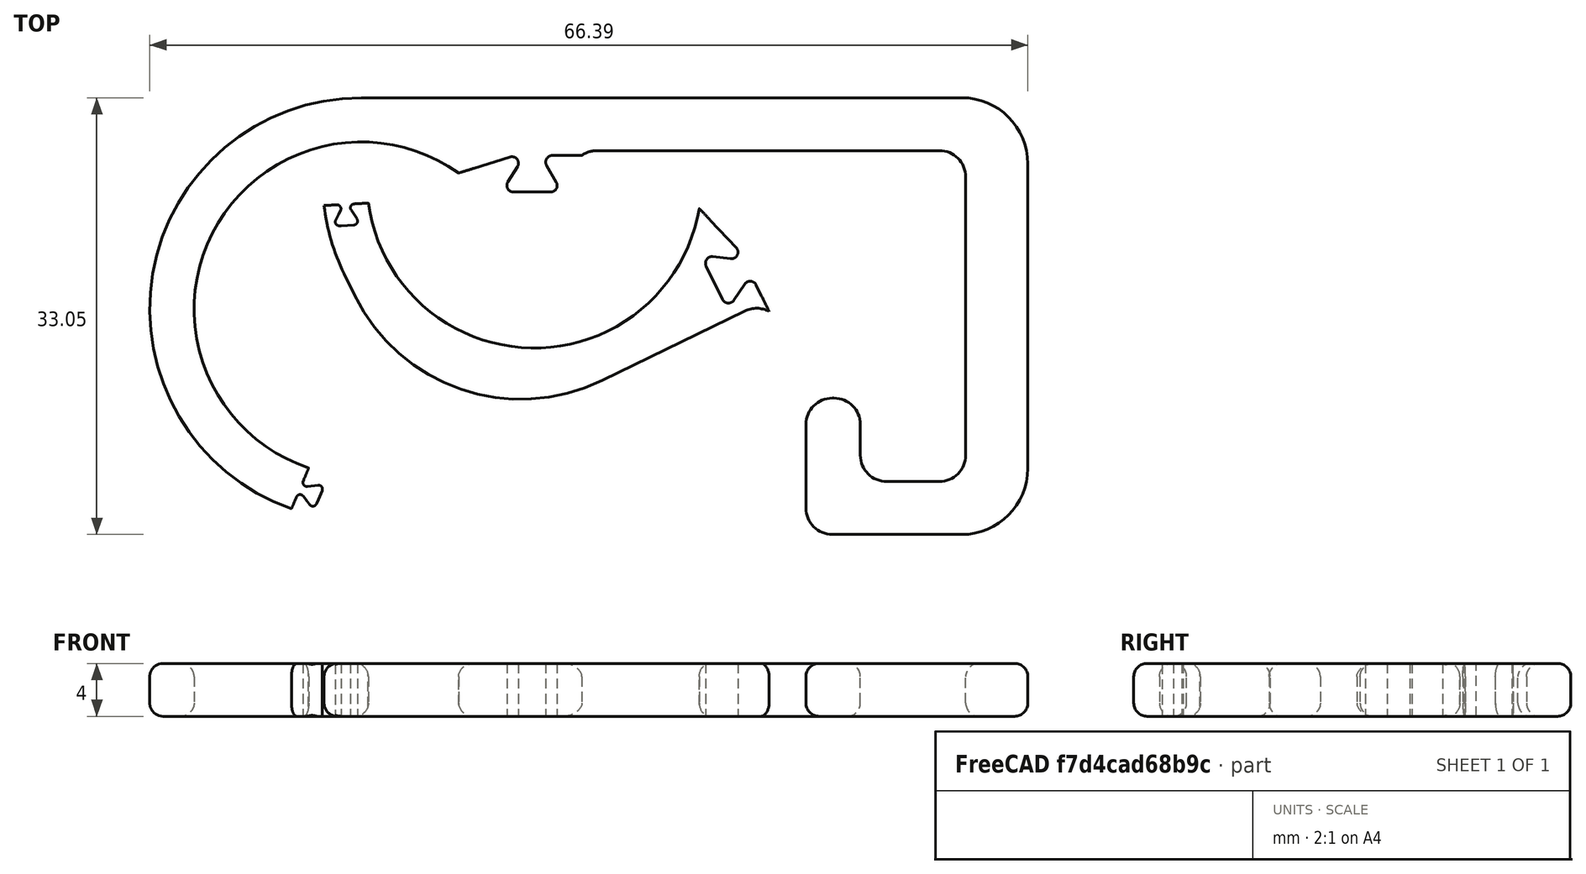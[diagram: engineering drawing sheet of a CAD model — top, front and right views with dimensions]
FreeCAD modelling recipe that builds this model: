
FCSTD DOCUMENT  (FreeCAD 0.20R29177 +233 (Git))
Label: Clotness hook
License: All rights reserved
LicenseURL: http://en.wikipedia.org/wiki/All_rights_reserved
objects: Part::FeaturePython×3, Sketcher::SketchObject×2, Part::Extrusion×2, Part::Fillet×1, App::DocumentObjectGroup×1, Mesh::Feature×1
note: 8 computed .brp shape members not serialized (recipe doc carries the construction recipe); baked Part::Feature solids carry a one-line shape summary decoded from their .brp

FEATURE [Sketcher::SketchObject] Sketch
  FullyConstrained = false
  sketch-geometry (23):
    g0: Circle CenterX=0 CenterY=0 CenterZ=0 NormalX=0 NormalY=0 NormalZ=1 AngleXU=0 Radius=12.65
    g1: ArcOfCircle CenterX=0 CenterY=0 CenterZ=0 NormalX=0 NormalY=0 NormalZ=1 AngleXU=0 Radius=16 StartAngle=1.5708 EndAngle=4.71239
    g2: LineSegment StartX=-2.6e-15 StartY=16 StartZ=0 EndX=45.3868 EndY=16 EndZ=0
    g3: LineSegment StartX=50.3868 StartY=11 StartZ=0 EndX=50.3868 EndY=-12.0462 EndZ=0
    g4: LineSegment StartX=45.3868 StartY=-17.0462 StartZ=0 EndX=35.6116 EndY=-17.0462 EndZ=0
    g5: LineSegment StartX=33.6116 StartY=-15.0462 StartZ=0 EndX=33.6116 EndY=-8.72342 EndZ=0
    g6: LineSegment StartX=35.6116 StartY=-6.72342 StartZ=0 EndX=35.7276 EndY=-6.72342 EndZ=0
    g7: LineSegment StartX=37.7276 StartY=-8.72342 StartZ=0 EndX=37.7276 EndY=-11.0462 EndZ=0
    g8: LineSegment StartX=39.7276 StartY=-13.0462 StartZ=0 EndX=43.6896 EndY=-13.0462 EndZ=0
    g9: LineSegment StartX=45.6896 StartY=-11.0462 StartZ=0 EndX=45.6896 EndY=10 EndZ=0
    g10: LineSegment StartX=43.6896 StartY=12 StartZ=0 EndX=17.8303 EndY=12 EndZ=0
    g11: LineSegment StartX=15.8303 StartY=10 StartZ=0 EndX=15.8303 EndY=-2 EndZ=0
    g12: LineSegment StartX=1.83034 StartY=-16 StartZ=0 EndX=1.13e-14 EndY=-16 EndZ=0
    g13: ArcOfCircle CenterX=1.83034 CenterY=-2 CenterZ=0 NormalX=0 NormalY=0 NormalZ=1 AngleXU=0 Radius=14 StartAngle=4.71239 EndAngle=6.28319
    g14: ArcOfCircle CenterX=17.8303 CenterY=10 CenterZ=0 NormalX=0 NormalY=0 NormalZ=1 AngleXU=0 Radius=2 StartAngle=1.5708 EndAngle=3.14159
    g15: ArcOfCircle CenterX=43.6896 CenterY=10 CenterZ=0 NormalX=0 NormalY=0 NormalZ=1 AngleXU=0 Radius=2 StartAngle=3e-16 EndAngle=1.5708
    g16: ArcOfCircle CenterX=43.6896 CenterY=-11.0462 CenterZ=0 NormalX=0 NormalY=0 NormalZ=1 AngleXU=0 Radius=2 StartAngle=4.71239 EndAngle=6.28319
    g17: ArcOfCircle CenterX=39.7276 CenterY=-11.0462 CenterZ=0 NormalX=0 NormalY=0 NormalZ=1 AngleXU=0 Radius=2 StartAngle=3.14159 EndAngle=4.71239
    g18: ArcOfCircle CenterX=35.7276 CenterY=-8.72342 CenterZ=0 NormalX=0 NormalY=0 NormalZ=1 AngleXU=0 Radius=2 StartAngle=-9e-16 EndAngle=1.5708
    g19: ArcOfCircle CenterX=35.6116 CenterY=-8.72342 CenterZ=0 NormalX=0 NormalY=0 NormalZ=1 AngleXU=0 Radius=2 StartAngle=1.5708 EndAngle=3.14159
    g20: ArcOfCircle CenterX=35.6116 CenterY=-15.0462 CenterZ=0 NormalX=0 NormalY=0 NormalZ=1 AngleXU=0 Radius=2 StartAngle=3.14159 EndAngle=4.71239
    g21: ArcOfCircle CenterX=45.3868 CenterY=-12.0462 CenterZ=0 NormalX=0 NormalY=0 NormalZ=1 AngleXU=0 Radius=5 StartAngle=4.71239 EndAngle=6.28319
    g22: ArcOfCircle CenterX=45.3868 CenterY=11 CenterZ=0 NormalX=0 NormalY=0 NormalZ=1 AngleXU=0 Radius=5 StartAngle=0 EndAngle=1.5708
  constraints (49):
    c: Coincident(g0,g-1)
    c: Diameter(g0) = 25.3
    c: Coincident(g1,g0)
    c: Tangent(g1,g2) = 1.5708
    c: Vertical(g3)
    c: Horizontal(g4)
    c: Vertical(g5)
    c: Horizontal(g6)
    c: Vertical(g7)
    c: Horizontal(g8)
    c: Vertical(g9)
    c: Horizontal(g10)
    c: Vertical(g11)
    c: Coincident(g12,g1)
    c: Horizontal(g12)
    c: Horizontal(g2)
    c: Radius(g1) = 16
    c: Tangent(g11,g13) = 1.5708
    c: Tangent(g12,g13) = 1.5708
    c: Tangent(g10,g14) = -1.5708
    c: Tangent(g11,g14) = -1.5708
    c: Tangent(g9,g15) = -1.5708
    c: Tangent(g10,g15) = -1.5708
    c: Tangent(g8,g16) = -1.5708
    c: Tangent(g9,g16) = -1.5708
    c: Tangent(g7,g17) = -1.5708
    c: Tangent(g8,g17) = -1.5708
    c: Tangent(g6,g18) = 1.5708
    c: Tangent(g7,g18) = 1.5708
    c: Tangent(g5,g19) = 1.5708
    c: Tangent(g6,g19) = 1.5708
    c: Tangent(g4,g20) = 1.5708
    c: Tangent(g5,g20) = 1.5708
    c: Tangent(g3,g21) = 1.5708
    c: Tangent(g4,g21) = 1.5708
    c: Tangent(g2,g22) = 1.5708
    c: Tangent(g3,g22) = 1.5708
    c: Radius(g20) = 2
    c: Radius(g19) = 2
    c: Radius(g18) = 2
    c: Radius(g17) = 2
    c: Radius(g16) = 2
    c: Radius(g15) = 2
    c: Radius(g22) = 5
    c: Radius(g21) = 5
    c: Radius(g13) = 14
    c: Radius(g14) = 2
    c: DistanceY(g10,g2) = 4
    c: DistanceY(g4,g8) = 4
FEATURE [Sketcher::SketchObject] Sketch001
  FullyConstrained = false
  MapMode = 2
  Support = -> [Sketch]
  sketch-geometry (19):
    g0: LineSegment StartX=7.35739 StartY=10.3021 StartZ=0 EndX=-3.9965 EndY=-12.0403 EndZ=0
    g1: LineSegment StartX=-3.9965 StartY=-12.0403 StartZ=0 EndX=-4.39779 EndY=-12.9962 EndZ=0
    g2: LineSegment StartX=-4.08343 StartY=-13.4099 StartZ=0 EndX=-3.2887 EndY=-13.3091 EndZ=0
    g3: LineSegment StartX=-2.97434 StartY=-13.7229 StartZ=0 EndX=-3.39416 EndY=-14.7229 EndZ=0
    g4: LineSegment StartX=-3.90965 StartY=-14.7883 StartZ=0 EndX=-4.39744 EndY=-14.1463 EndZ=0
    g5: LineSegment StartX=-4.91293 StartY=-14.2117 StartZ=0 EndX=-6.46781 EndY=-17.9156 EndZ=0
    g6: LineSegment StartX=7.35739 StartY=10.3021 StartZ=0 EndX=11.231 EndY=11.5121 EndZ=0
    g7: LineSegment StartX=11.801 StartY=10.7651 StartZ=0 EndX=11.0745 EndY=9.63137 EndZ=0
    g8: LineSegment StartX=11.4955 StartY=8.8616 StartZ=0 EndX=14.3029 EndY=8.8616 EndZ=0
    g9: LineSegment StartX=14.7359 StartY=9.6116 StartZ=0 EndX=14.004 EndY=10.8794 EndZ=0
    g10: LineSegment StartX=14.437 StartY=11.6294 StartZ=0 EndX=20.3712 EndY=11.6294 EndZ=0
    g11: ArcOfCircle CenterX=-3.25095 CenterY=-13.6068 CenterZ=0 NormalX=0 NormalY=0 NormalZ=1 AngleXU=0 Radius=0.3 StartAngle=5.88573 EndAngle=7.98013
    g12: ArcOfCircle CenterX=-3.67078 CenterY=-14.6068 CenterZ=0 NormalX=0 NormalY=0 NormalZ=1 AngleXU=0 Radius=0.3 StartAngle=3.79134 EndAngle=5.88573
    g13: ArcOfCircle CenterX=-4.63631 CenterY=-14.3278 CenterZ=0 NormalX=0 NormalY=0 NormalZ=1 AngleXU=0 Radius=0.3 StartAngle=0.649743 EndAngle=2.74414
    g14: ArcOfCircle CenterX=-4.12118 CenterY=-13.1123 CenterZ=0 NormalX=0 NormalY=0 NormalZ=1 AngleXU=0 Radius=0.3 StartAngle=2.74414 EndAngle=4.83853
    g15: ArcOfCircle CenterX=11.3801 CenterY=11.0349 CenterZ=0 NormalX=0 NormalY=0 NormalZ=1 AngleXU=0 Radius=0.5 StartAngle=5.71329 EndAngle=8.15675
    g16: ArcOfCircle CenterX=11.4955 CenterY=9.3616 CenterZ=0 NormalX=0 NormalY=0 NormalZ=1 AngleXU=0 Radius=0.5 StartAngle=2.5717 EndAngle=4.71239
    g17: ArcOfCircle CenterX=14.3029 CenterY=9.3616 CenterZ=0 NormalX=0 NormalY=0 NormalZ=1 AngleXU=0 Radius=0.5 StartAngle=4.71239 EndAngle=6.80678
    g18: ArcOfCircle CenterX=14.437 CenterY=11.1294 CenterZ=0 NormalX=0 NormalY=0 NormalZ=1 AngleXU=0 Radius=0.5 StartAngle=1.5708 EndAngle=3.66519
  constraints (34):
    c: Coincident(g0,g1)
    c: Coincident(g0,g6)
    c: Horizontal(g8)
    c: Horizontal(g10)
    c: Angle(g2,g1) = 1.0472
    c: Angle(g5,g4) = 1.0472
    c: Parallel(g1,g5)
    c: Parallel(g3,g5)
    c: Angle(g6,g7) = 0.698132
    c: Angle(g9,g10) = 1.0472
    c: Tangent(g2,g11) = 1.5708
    c: Tangent(g3,g11) = 1.5708
    c: Tangent(g3,g12) = 1.5708
    c: Tangent(g4,g12) = 1.5708
    c: Tangent(g4,g13) = -1.5708
    c: Tangent(g5,g13) = -1.5708
    c: Tangent(g1,g14) = -1.5708
    c: Tangent(g2,g14) = -1.5708
    c: Tangent(g6,g15) = 1.5708
    c: Tangent(g7,g15) = 1.5708
    c: Tangent(g7,g16) = -1.5708
    c: Tangent(g8,g16) = -1.5708
    c: Tangent(g8,g17) = -1.5708
    c: Tangent(g9,g17) = -1.5708
    c: Tangent(g9,g18) = 1.5708
    c: Tangent(g10,g18) = 1.5708
    c: Radius(g15) = 0.5
    c: Radius(g16) = 0.5
    c: Radius(g17) = 0.5
    c: Radius(g18) = 0.5
    c: Radius(g14) = 0.3
    c: Radius(g11) = 0.3
    c: Radius(g12) = 0.3
    c: Radius(g13) = 0.3
FEATURE [Part::Extrusion] Extrude
  Base = -> Sketch
  Dir = (0,0,1)
  DirMode = 2
  FaceMakerClass = Part::FaceMakerBullseye
  LengthFwd = 4
  LengthRev = 0
  Solid = true
  Symmetric = false
FEATURE [Part::Fillet] Fillet
  Base = -> Extrude
  Edges = 46 edges r=1: [Edge3,Edge4,Edge6,Edge7,Edge9,Edge10,Edge12,Edge13,Edge15,Edge16,Edge18,Edge19,Edge21,Edge22,Edge24,Edge25,Edge27,Edge28,Edge30,Edge31,Edge33,Edge34,Edge36,Edge37,Edge39,Edge40,Edge42,Edge43,Edge45,Edge46,Edge48,Edge49,Edge51,Edge52,Edge54,Edge55,Edge57,Edge58,Edge60,Edge61,Edge63,Edge64,Edge65,+3 more]
FEATURE [Part::Extrusion] Extrude001
  Base = -> Sketch001
  Dir = (0,0,1)
  DirMode = 2
  FaceMakerClass = Part::FaceMakerBullseye
  LengthFwd = 12
  LengthRev = 0
  Placement = pos=(0,0,-2) rot=(0,0,1;0rad)
  Solid = false
  Symmetric = false
FEATURE [Part::FeaturePython] Slice  # WARN: FeaturePython — macro-defined, semantics opaque (R4)
  Base = -> Fillet
  Mode = 1
  Tolerance = 0
  Tools = -> [Extrude001]
FEATURE [Part::FeaturePython] Slice_child0  label="Slice.0"  # WARN: FeaturePython — macro-defined, semantics opaque (R4)
  Base = -> Slice
  FilterType = 1
  Invert = false
  OverrideMaxVal = 0
  WindowFrom = 80
  WindowTo = 100
  items = 0
FEATURE [Part::FeaturePython] Slice_child1  label="Slice.1"  # WARN: FeaturePython — macro-defined, semantics opaque (R4)
  Base = -> Slice
  FilterType = 1
  Invert = false
  OverrideMaxVal = 0
  Placement = pos=(13.0656,9.71032,0) rot=(0,0,-1;1.11701rad)
  WindowFrom = 80
  WindowTo = 100
  items = 1
FEATURE [App::DocumentObjectGroup] GrExplode_Slice  label="Exploded Slice"
  Group = -> [Slice_child0,Slice_child1]
FEATURE [Mesh::Feature] Mesh  label="Exploded Slice (Meshed)"
